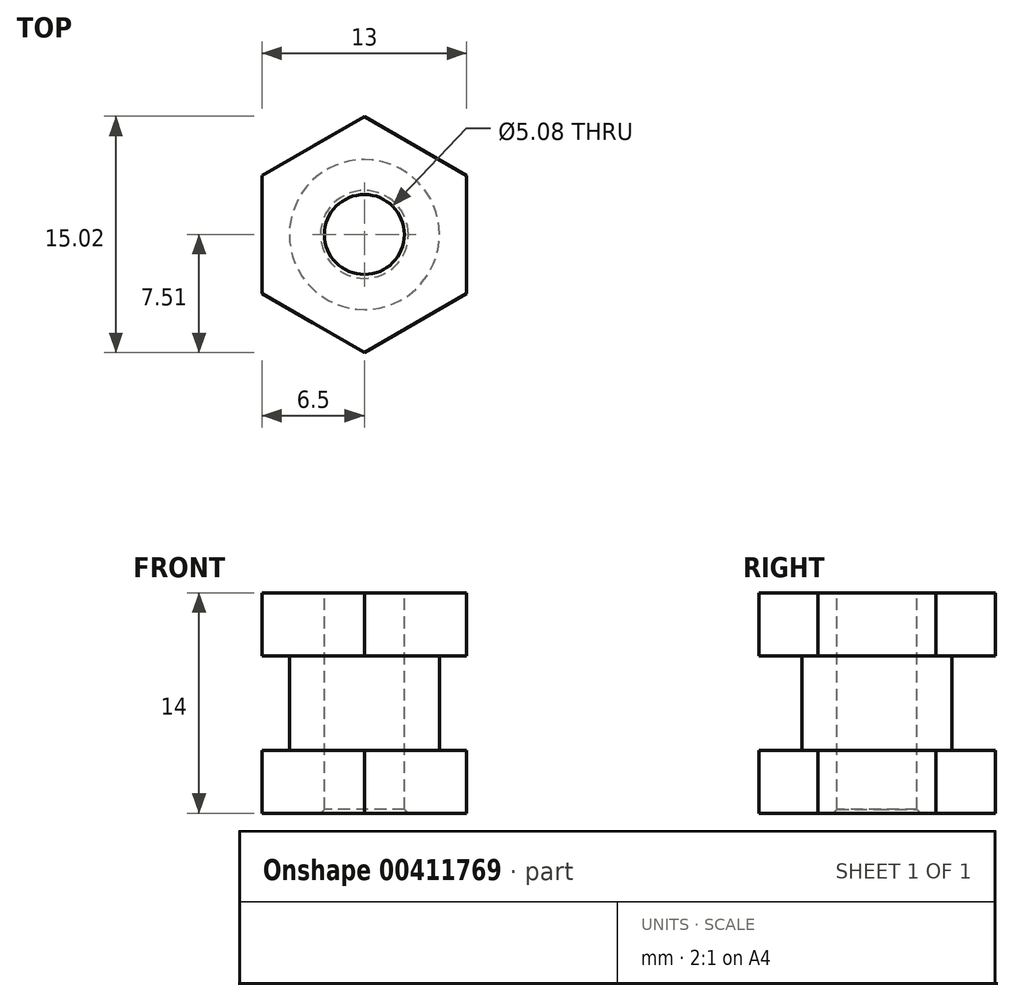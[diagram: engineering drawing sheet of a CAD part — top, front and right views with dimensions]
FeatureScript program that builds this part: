
annotation { "Feature Type Name" : "Feature", "Feature Type Description" : "" }
export const myFeature = defineFeature(function(context is Context, id is Id, definition is map)
    precondition{}
    {
        {
            var Q0;
            Q0=qCreatedBy(makeId("Top.planeOp"),FACE);
            var sketch = newSketch(context, id + "F0", { "sketchPlane" : qUnion([Q0])});
            skCircle(sketch, "E0.cCircle", {"center": v(0, 0) * mm, "radius": 6.5 * mm, "construction": true});
            skLineSegment(sketch, "E0.0", {"start": v(-6.5, 3.75) * mm, "end": v(0, 7.5) * mm});
            skLineSegment(sketch, "E0.1", {"start": v(0, 7.5) * mm, "end": v(6.5, 3.75) * mm});
            skLineSegment(sketch, "E0.2", {"start": v(6.5, 3.75) * mm, "end": v(6.5, -3.75) * mm});
            skLineSegment(sketch, "E0.3", {"start": v(6.5, -3.75) * mm, "end": v(0, -7.5) * mm});
            skLineSegment(sketch, "E0.4", {"start": v(0, -7.5) * mm, "end": v(-6.5, -3.75) * mm});
            skLineSegment(sketch, "E0.5", {"start": v(-6.5, -3.75) * mm, "end": v(-6.5, 3.75) * mm});
            skPoint(sketch, "E0.0.midPoint", {"position": v(-3.25, 5.63) * mm});
            skSolve(sketch);
        }
        {
            var Q0;
            Q0=makeQuery(id+"F0.imprint","IMPRINT",FACE,{"disambiguationData":[TD([[makeQuery(id+"F0.imprint","IMPRINT",EDGE,{"derivedFrom":sQuery(id+"F0.wireOp",EDGE,"E0.0")}),-1.0]])]});
            extrude(context, id + "F1", {"entities" : qUnion([Q0]), "depth" : 4 * mm, "offsetDistance" : 25 * mm});
        }
        {
            var Q0;
            Q0=makeQuery(id+"F1.opExtrude","CAP_FACE",FACE,{"disambiguationData":[OSD([sQuery(id+"F0.wireOp",EDGE,"E0.0"),sQuery(id+"F0.wireOp",EDGE,"E0.1"),sQuery(id+"F0.wireOp",EDGE,"E0.2"),sQuery(id+"F0.wireOp",EDGE,"E0.3"),sQuery(id+"F0.wireOp",EDGE,"E0.4"),sQuery(id+"F0.wireOp",EDGE,"E0.5")])],"isStart":false});
            var sketch = newSketch(context, id + "F2", { "sketchPlane" : qUnion([Q0])});
            skCircle(sketch, "E1", {"center": v(0, 0) * mm, "radius": 4.76 * mm});
            skSolve(sketch);
        }
        {
            var Q0;
            Q0=makeQuery(id+"F2.imprint","IMPRINT",FACE,{"disambiguationData":[TD([[makeQuery(id+"F2.imprint","IMPRINT",EDGE,{"derivedFrom":sQuery(id+"F2.wireOp",EDGE,"E1")}),1.0]])]});
            extrude(context, id + "F3", {"entities" : qUnion([Q0]), "operationType" : NewBodyOperationType.ADD, "depth" : 6 * mm, "offsetDistance" : 25 * mm});
        }
        {
            var Q0;
            Q0=makeQuery(id+"F3.opExtrude","CAP_FACE",FACE,{"disambiguationData":[OSD([sQuery(id+"F2.wireOp",EDGE,"E1")])],"isStart":false});
            var sketch = newSketch(context, id + "F4", { "sketchPlane" : qUnion([Q0])});
            skCircle(sketch, "E2.cCircle", {"center": v(0, 0) * mm, "radius": 6.5 * mm, "construction": true});
            skLineSegment(sketch, "E2.0", {"start": v(-6.5, -3.75) * mm, "end": v(-6.5, 3.75) * mm});
            skLineSegment(sketch, "E2.1", {"start": v(-6.5, 3.75) * mm, "end": v(0, 7.5) * mm});
            skLineSegment(sketch, "E2.2", {"start": v(0, 7.5) * mm, "end": v(6.5, 3.75) * mm});
            skLineSegment(sketch, "E2.3", {"start": v(6.5, 3.75) * mm, "end": v(6.5, -3.75) * mm});
            skLineSegment(sketch, "E2.4", {"start": v(6.5, -3.75) * mm, "end": v(0, -7.5) * mm});
            skLineSegment(sketch, "E2.5", {"start": v(0, -7.5) * mm, "end": v(-6.5, -3.75) * mm});
            skPoint(sketch, "E2.0.midPoint", {"position": v(-6.5, 0) * mm});
            skSolve(sketch);
        }
        {
            var Q0;
            Q0 = qSketchRegion(id + "F4", true);
            extrude(context, id + "F5", {"entities" : qUnion([Q0]), "operationType" : NewBodyOperationType.ADD, "depth" : 4 * mm, "offsetDistance" : 25 * mm});
        }
        {
            var Q0;
            Q0=makeQuery(id+"F5.opExtrude","CAP_FACE",FACE,{"disambiguationData":[OSD([sQuery(id+"F4.wireOp",EDGE,"E2.0"),sQuery(id+"F4.wireOp",EDGE,"E2.1"),sQuery(id+"F4.wireOp",EDGE,"E2.2"),sQuery(id+"F4.wireOp",EDGE,"E2.3"),sQuery(id+"F4.wireOp",EDGE,"E2.4"),sQuery(id+"F4.wireOp",EDGE,"E2.5")])],"isStart":false});
            var sketch = newSketch(context, id + "F6", { "sketchPlane" : qUnion([Q0])});
            skCircle(sketch, "E3", {"center": v(0, 0) * mm, "radius": 2.54 * mm});
            skSolve(sketch);
        }
        {
            var Q0;
            Q0=makeQuery(id+"F6.imprint","IMPRINT",FACE,{"disambiguationData":[TD([[makeQuery(id+"F6.imprint","IMPRINT",EDGE,{"derivedFrom":sQuery(id+"F6.wireOp",EDGE,"E3")}),1.0]])]});
            extrude(context, id + "F7", {"entities" : qUnion([Q0]), "operationType" : NewBodyOperationType.REMOVE, "oppositeDirection" : true, "depth" : 25 * mm, "offsetDistance" : 25 * mm});
        }
        {
            var Q0;
            Q0=makeQuery(id+"F7.boolean.opBoolean","COPY",EDGE,{"derivedFrom":makeQuery(id+"F7.opExtrude","CAP_EDGE",EDGE,{"disambiguationData":[OSD([sQuery(id+"F6.wireOp",EDGE,"E3")])],"isStart":true})});
            var Q1;
            Q1=makeQuery(id+"F7.boolean.opBoolean","INTERSECT",EDGE,{"derivedFrom":[makeQuery(id+"F1.opExtrude","CAP_FACE",FACE,{"disambiguationData":[OSD([sQuery(id+"F0.wireOp",EDGE,"E0.0"),sQuery(id+"F0.wireOp",EDGE,"E0.1"),sQuery(id+"F0.wireOp",EDGE,"E0.2"),sQuery(id+"F0.wireOp",EDGE,"E0.3"),sQuery(id+"F0.wireOp",EDGE,"E0.4"),sQuery(id+"F0.wireOp",EDGE,"E0.5")])],"isStart":true}),makeQuery(id+"F7.opExtrude","SWEPT_FACE",FACE,{"disambiguationData":[OSD([sQuery(id+"F6.wireOp",EDGE,"E3")])]})]});
            chamfer(context, id + "F8", {"entities" : qUnion([Q0, Q1]), "width" : 0.25 * mm, "tangentPropagation" : true});
        }
    });
